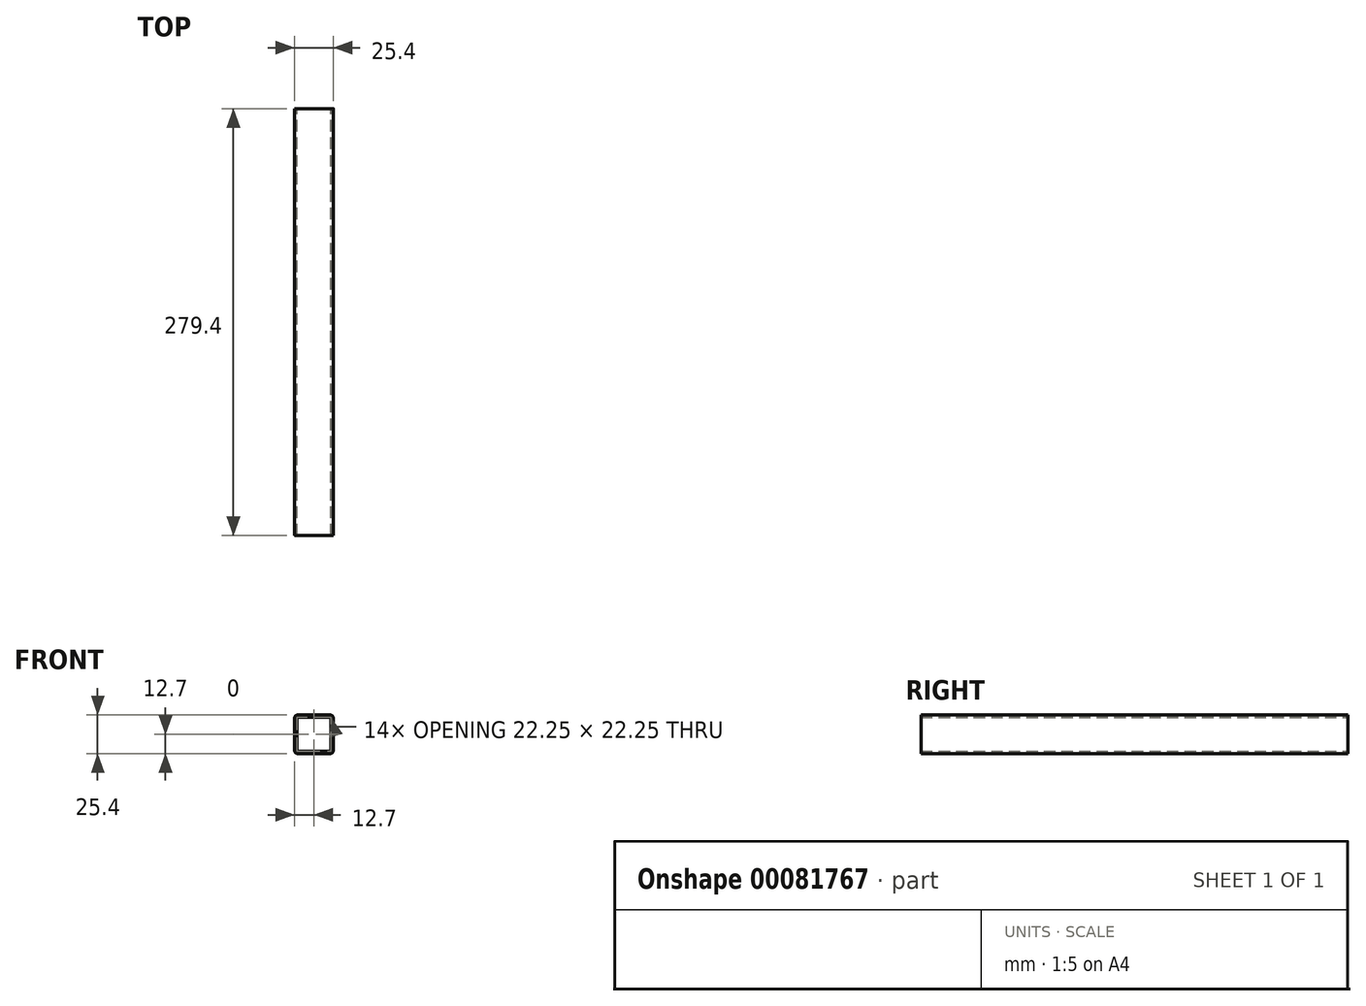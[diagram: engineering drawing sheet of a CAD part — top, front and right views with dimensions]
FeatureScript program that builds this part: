
annotation { "Feature Type Name" : "Feature", "Feature Type Description" : "" }
export const myFeature = defineFeature(function(context is Context, id is Id, definition is map)
    precondition{}
    {
        {
            var Q0;
            Q0=qCreatedBy(makeId("Front.planeOp"),FACE);
            var sketch = newSketch(context, id + "F0", { "sketchPlane" : qUnion([Q0])});
            skLineSegment(sketch, "E0.bottom", {"start": v(-10.62, -12.7) * mm, "end": v(10.62, -12.7) * mm});
            skLineSegment(sketch, "E0.top", {"start": v(-10.62, 12.7) * mm, "end": v(10.62, 12.7) * mm});
            skLineSegment(sketch, "E0.left", {"start": v(-12.7, -10.62) * mm, "end": v(-12.7, 10.62) * mm});
            skLineSegment(sketch, "E0.right", {"start": v(12.7, -10.62) * mm, "end": v(12.7, 10.62) * mm});
            skPoint(sketch, "E0.middle", {"position": v(0, 0) * mm});
            skLineSegment(sketch, "E1.bottom", {"start": v(10.62, -11.13) * mm, "end": v(-10.62, -11.13) * mm});
            skLineSegment(sketch, "E1.top", {"start": v(10.62, 11.13) * mm, "end": v(-10.62, 11.13) * mm});
            skLineSegment(sketch, "E1.left", {"start": v(11.13, -10.62) * mm, "end": v(11.13, 10.62) * mm});
            skLineSegment(sketch, "E1.right", {"start": v(-11.13, -10.62) * mm, "end": v(-11.13, 10.62) * mm});
            skPoint(sketch, "E2.visualSharp", {"position": v(-11.13, 11.13) * mm});
            skArc(sketch, "E2.filletArc", {"start": v(-10.62, 11.13) * mm, "mid": v(-10.98, 10.98) * mm, "end": v(-11.13, 10.62) * mm});
            skPoint(sketch, "E3.visualSharp", {"position": v(11.13, 11.13) * mm});
            skArc(sketch, "E3.filletArc", {"start": v(11.13, 10.62) * mm, "mid": v(10.98, 10.98) * mm, "end": v(10.62, 11.13) * mm});
            skPoint(sketch, "E4.visualSharp", {"position": v(11.13, -11.13) * mm});
            skArc(sketch, "E4.filletArc", {"start": v(10.62, -11.13) * mm, "mid": v(10.98, -10.98) * mm, "end": v(11.13, -10.62) * mm});
            skPoint(sketch, "E5.visualSharp", {"position": v(-11.13, -11.13) * mm});
            skArc(sketch, "E5.filletArc", {"start": v(-11.13, -10.62) * mm, "mid": v(-10.98, -10.98) * mm, "end": v(-10.62, -11.13) * mm});
            skPoint(sketch, "E6.visualSharp", {"position": v(-12.7, 12.7) * mm});
            skArc(sketch, "E6.filletArc", {"start": v(-10.62, 12.7) * mm, "mid": v(-12.09, 12.09) * mm, "end": v(-12.7, 10.62) * mm});
            skPoint(sketch, "E7.visualSharp", {"position": v(12.7, 12.7) * mm});
            skArc(sketch, "E7.filletArc", {"start": v(12.7, 10.62) * mm, "mid": v(12.09, 12.09) * mm, "end": v(10.62, 12.7) * mm});
            skPoint(sketch, "E8.visualSharp", {"position": v(-12.7, -12.7) * mm});
            skArc(sketch, "E8.filletArc", {"start": v(-12.7, -10.62) * mm, "mid": v(-12.09, -12.09) * mm, "end": v(-10.62, -12.7) * mm});
            skPoint(sketch, "E9.visualSharp", {"position": v(12.7, -12.7) * mm});
            skArc(sketch, "E9.filletArc", {"start": v(10.62, -12.7) * mm, "mid": v(12.09, -12.09) * mm, "end": v(12.7, -10.62) * mm});
            skSolve(sketch);
        }
        {
            var Q0;
            Q0=qSketchRegion(id+"F0",true);
            extrude(context, id + "F1", {"entities" : qUnion([Q0]), "depth" : 279.4 * mm});
        }
    });
